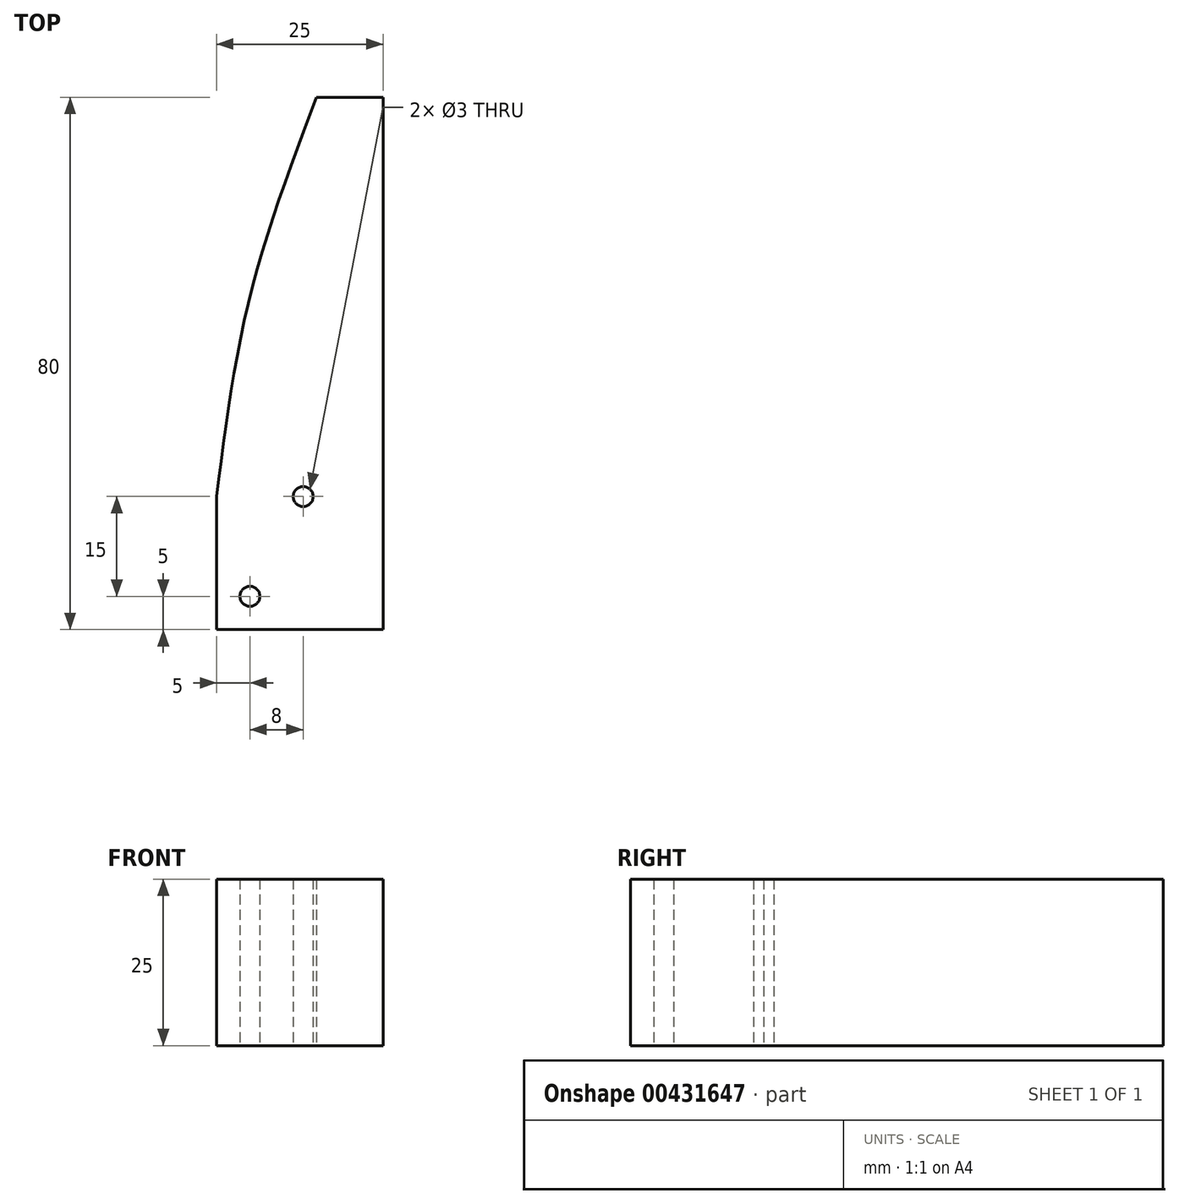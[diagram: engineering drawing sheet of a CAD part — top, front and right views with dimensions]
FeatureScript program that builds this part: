
annotation { "Feature Type Name" : "Feature", "Feature Type Description" : "" }
export const myFeature = defineFeature(function(context is Context, id is Id, definition is map)
    precondition{}
    {
        {
            var Q0;
            Q0=qCreatedBy(makeId("Top.planeOp"),FACE);
            var sketch = newSketch(context, id + "F0", { "sketchPlane" : qUnion([Q0])});
            skLineSegment(sketch, "E0", {"start": v(0, 0) * mm, "end": v(0, 60) * mm});
            skLineSegment(sketch, "E1", {"start": v(-10, 60) * mm, "end": v(0, 60) * mm});
            skLineSegment(sketch, "E2", {"start": v(0, 0) * mm, "end": v(-25, 0) * mm, "construction": true});
            skLineSegment(sketch, "E3", {"start": v(0, 30) * mm, "end": v(-20, 30) * mm, "construction": true});
            skFitSpline(sketch, "E4", {"points": [v(-10, 60) * mm, v(-20, 30) * mm, v(-25, 0) * mm], "startDerivative": vector(-22.26, -59.13) * mm, "endDerivative": vector(-7.7, -60.88) * mm});
            skLineSegment(sketch, "E5", {"start": v(-25, 0) * mm, "end": v(-25, -20) * mm});
            skLineSegment(sketch, "E6", {"start": v(-25, -20) * mm, "end": v(0, -20) * mm});
            skLineSegment(sketch, "E7", {"start": v(0, -20) * mm, "end": v(0, 0) * mm});
            skLineSegment(sketch, "E8.bottom", {"start": v(-25, -20) * mm, "end": v(-20, -20) * mm, "construction": true});
            skLineSegment(sketch, "E8.top", {"start": v(-25, -15) * mm, "end": v(-20, -15) * mm, "construction": true});
            skLineSegment(sketch, "E8.left", {"start": v(-25, -20) * mm, "end": v(-25, -15) * mm, "construction": true});
            skLineSegment(sketch, "E8.right", {"start": v(-20, -20) * mm, "end": v(-20, -15) * mm, "construction": true});
            skLineSegment(sketch, "E9.bottom", {"start": v(0, 0) * mm, "end": v(-12, 0) * mm, "construction": true});
            skLineSegment(sketch, "E9.top", {"start": v(0, 0) * mm, "end": v(-12, 0) * mm, "construction": true});
            skLineSegment(sketch, "E9.left", {"start": v(0, 0) * mm, "end": v(0, 0) * mm});
            skLineSegment(sketch, "E9.right", {"start": v(-12, 0) * mm, "end": v(-12, 0) * mm});
            skCircle(sketch, "E10", {"center": v(-12, 0) * mm, "radius": 1.5 * mm});
            skCircle(sketch, "E11", {"center": v(-20, -15) * mm, "radius": 1.5 * mm});
            skSolve(sketch);
        }
        {
            var Q0;
            Q0=makeQuery(id+"F0.imprint","IMPRINT",FACE,{"disambiguationData":[TD([[makeQuery(id+"F0.imprint","IMPRINT",EDGE,{"derivedFrom":sQuery(id+"F0.wireOp",EDGE,"E0")}),1.0]])]});
            extrude(context, id + "F1", {"entities" : qUnion([Q0]), "depth" : 25 * mm});
        }
    });
